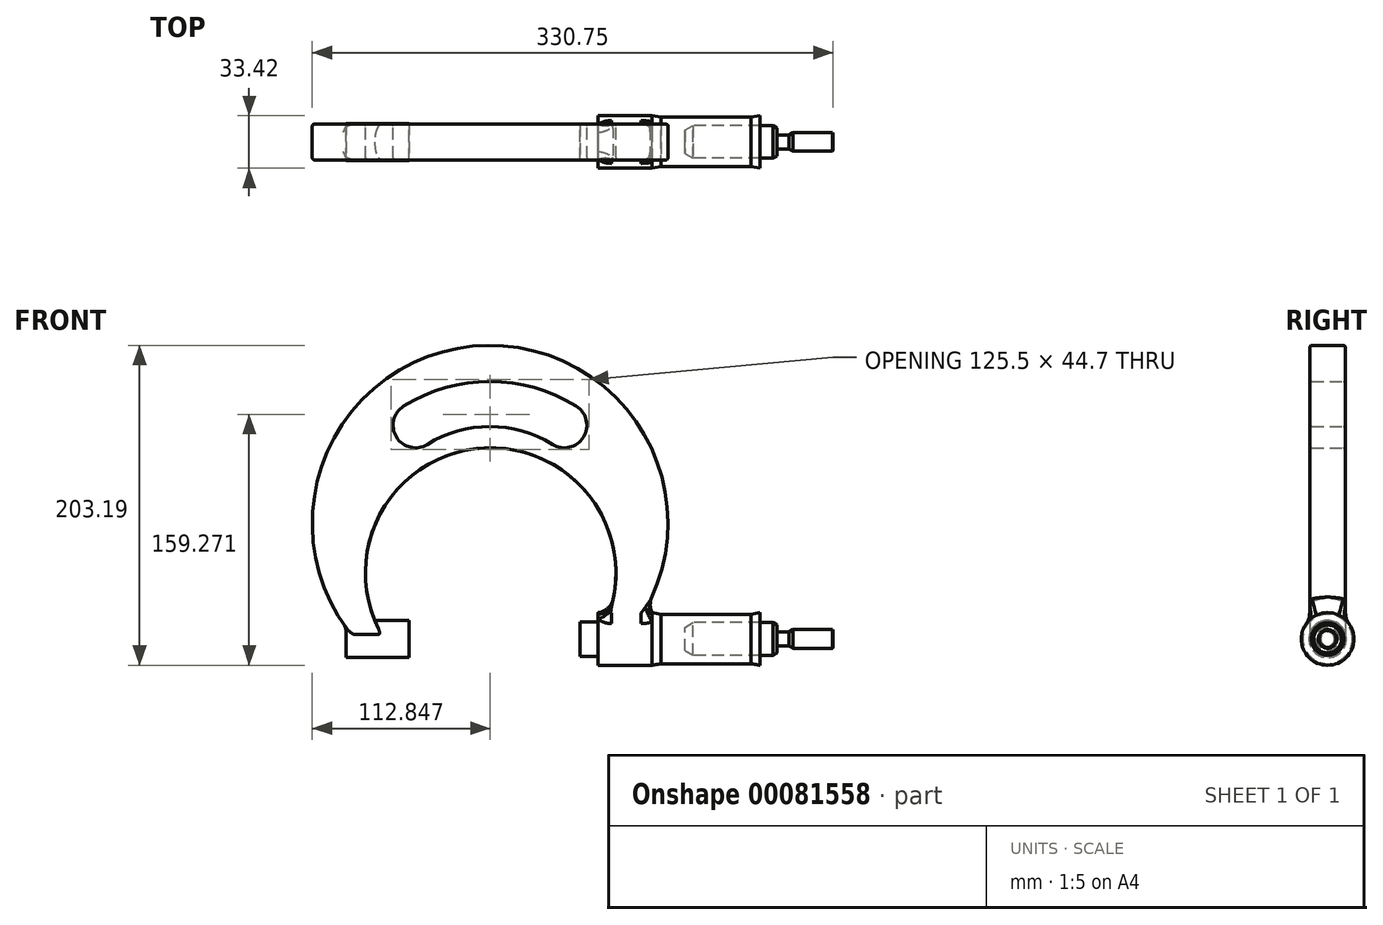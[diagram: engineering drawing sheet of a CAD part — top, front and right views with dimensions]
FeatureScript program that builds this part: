
annotation { "Feature Type Name" : "Feature", "Feature Type Description" : "" }
export const myFeature = defineFeature(function(context is Context, id is Id, definition is map)
    precondition{}
    {
        {
            var Q0;
            Q0=qCreatedBy(makeId("Front.planeOp"),FACE);
            var sketch = newSketch(context, id + "F0", { "sketchPlane" : qUnion([Q0])});
            skArc(sketch, "E0", {"start": v(0, 0) * mm, "mid": v(-38.1, 82.88) * mm, "end": v(-76.2, 0) * mm});
            skArc(sketch, "E1", {"start": v(-7.9, 0) * mm, "mid": v(-37.96, 53.97) * mm, "end": v(-68.04, 0) * mm});
            skLineSegment(sketch, "E2", {"start": v(-76.2, 0) * mm, "end": v(-68.04, 0) * mm});
            skLineSegment(sketch, "E3", {"start": v(-7.9, 0) * mm, "end": v(0, 0) * mm});
            skLineSegment(sketch, "E4.bottom", {"start": v(-76.2, 0) * mm, "end": v(-67.8, 0) * mm});
            skLineSegment(sketch, "E5", {"start": v(-38.1, 69.98) * mm, "end": v(-37.96, -37.66) * mm, "construction": true});
            skLineSegment(sketch, "E6", {"start": v(-89.8, 60.32) * mm, "end": v(20.51, 60.32) * mm, "construction": true});
            skArc(sketch, "E7", {"start": v(-17.15, 60.32) * mm, "mid": v(-38.14, 66.3) * mm, "end": v(-59.14, 60.32) * mm});
            skArc(sketch, "E8.0.startCap", {"start": v(-13.8, 65.71) * mm, "mid": v(-11.75, 56.97) * mm, "end": v(-20.5, 54.93) * mm});
            skArc(sketch, "E8.0.endCap", {"start": v(-55.79, 54.93) * mm, "mid": v(-64.53, 56.97) * mm, "end": v(-62.5, 65.71) * mm});
            skArc(sketch, "E8.0.left", {"start": v(-20.5, 54.93) * mm, "mid": v(-38.14, 59.96) * mm, "end": v(-55.79, 54.93) * mm});
            skArc(sketch, "E8.0.right", {"start": v(-13.8, 65.71) * mm, "mid": v(-38.14, 72.66) * mm, "end": v(-62.5, 65.71) * mm});
            skSolve(sketch);
        }
        {
            var Q0;
            Q0 = qSketchRegion(id + "F0", true);
            extrude(context, id + "F1", {"entities" : qUnion([Q0]), "depth" : 5.08 * mm, "hasSecondDirection" : true, "secondDirectionOppositeDirection" : true, "secondDirectionDepth" : 5.08 * mm});
        }
        {
            var Q0;
            Q0=makeQuery(id+"F1.opExtrude","CAP_FACE",FACE,{"disambiguationData":[OSD([sQuery(id+"F0.wireOp",EDGE,"E0"),sQuery(id+"F0.wireOp",EDGE,"E1"),sQuery(id+"F0.wireOp",EDGE,"E4.bottom"),sQuery(id+"F0.wireOp",EDGE,"E4.top"),sQuery(id+"F0.wireOp",EDGE,"E4.left"),sQuery(id+"F0.wireOp",EDGE,"E4.right"),sQuery(id+"F0.wireOp",EDGE,"VIkeURCC-5Tp6-DDTl-tPK2-hxNMprlm5AdZ.top"),sQuery(id+"F0.wireOp",EDGE,"VIkeURCC-5Tp6-DDTl-tPK2-hxNMprlm5AdZ.left"),sQuery(id+"F0.wireOp",EDGE,"VIkeURCC-5Tp6-DDTl-tPK2-hxNMprlm5AdZ.right"),sQuery(id+"F0.wireOp",EDGE,"E8.0.startCap"),sQuery(id+"F0.wireOp",EDGE,"E8.0.endCap"),sQuery(id+"F0.wireOp",EDGE,"E8.0.left"),sQuery(id+"F0.wireOp",EDGE,"E8.0.right")])],"isStart":true});
            var Q1;
            Q1=makeQuery(id+"F1.opExtrude","CAP_FACE",FACE,{"disambiguationData":[OSD([sQuery(id+"F0.wireOp",EDGE,"E0"),sQuery(id+"F0.wireOp",EDGE,"E1"),sQuery(id+"F0.wireOp",EDGE,"E4.bottom"),sQuery(id+"F0.wireOp",EDGE,"E4.top"),sQuery(id+"F0.wireOp",EDGE,"E4.left"),sQuery(id+"F0.wireOp",EDGE,"E4.right"),sQuery(id+"F0.wireOp",EDGE,"VIkeURCC-5Tp6-DDTl-tPK2-hxNMprlm5AdZ.top"),sQuery(id+"F0.wireOp",EDGE,"VIkeURCC-5Tp6-DDTl-tPK2-hxNMprlm5AdZ.left"),sQuery(id+"F0.wireOp",EDGE,"VIkeURCC-5Tp6-DDTl-tPK2-hxNMprlm5AdZ.right"),sQuery(id+"F0.wireOp",EDGE,"E8.0.startCap"),sQuery(id+"F0.wireOp",EDGE,"E8.0.endCap"),sQuery(id+"F0.wireOp",EDGE,"E8.0.left"),sQuery(id+"F0.wireOp",EDGE,"E8.0.right")])],"isStart":false});
            fillet(context, id + "F2", {"entities" : qUnion([Q0, Q1]), "radius" : 0.64 * mm, "tangentPropagation" : true, "allowEdgeOverflow" : false});
        }
        {
            var Q0;
            Q0=qCreatedBy(makeId("Right.planeOp"),FACE);
            var sketch = newSketch(context, id + "F3", { "sketchPlane" : qUnion([Q0])});
            skCircle(sketch, "E9", {"center": v(0, 0) * mm, "radius": 7.43 * mm});
            skSolve(sketch);
        }
        {
            var Q0;
            Q0 = qSketchRegion(id + "F3", true);
            extrude(context, id + "F4", {"entities" : qUnion([Q0]), "operationType" : NewBodyOperationType.ADD, "depth" : 7.62 * mm, "hasSecondDirection" : true, "secondDirectionOppositeDirection" : true, "secondDirectionDepth" : 7.62 * mm});
        }
        {
            var Q0;
            Q0=makeQuery(id+"F4.boolean.opBoolean","INTERSECT",EDGE,{"derivedFrom":[makeQuery(id+"F1.opExtrude","SWEPT_FACE",FACE,{"disambiguationData":[OSD([sQuery(id+"F0.wireOp",EDGE,"E0")])]}),makeQuery(id+"F4.opExtrude","SWEPT_FACE",FACE,{"disambiguationData":[OSD([sQuery(id+"F3.wireOp",EDGE,"E9")])]})]});
            var Q1;
            Q1=makeQuery(id+"F4.boolean.opBoolean","INTERSECT",EDGE,{"derivedFrom":[makeQuery(id+"F1.opExtrude","CAP_FACE",FACE,{"disambiguationData":[OSD([sQuery(id+"F0.wireOp",EDGE,"E0"),sQuery(id+"F0.wireOp",EDGE,"E1"),sQuery(id+"F0.wireOp",EDGE,"E4.bottom"),sQuery(id+"F0.wireOp",EDGE,"E3"),sQuery(id+"F0.wireOp",EDGE,"E8.0.startCap"),sQuery(id+"F0.wireOp",EDGE,"E8.0.endCap"),sQuery(id+"F0.wireOp",EDGE,"E8.0.left"),sQuery(id+"F0.wireOp",EDGE,"E8.0.right")])],"isStart":true}),makeQuery(id+"F4.opExtrude","SWEPT_FACE",FACE,{"disambiguationData":[OSD([sQuery(id+"F3.wireOp",EDGE,"E9")])]})]});
            var Q2;
            Q2=makeQuery(id+"F4.boolean.opBoolean","INTERSECT",EDGE,{"derivedFrom":[makeQuery(id+"F1.opExtrude","SWEPT_FACE",FACE,{"disambiguationData":[OSD([sQuery(id+"F0.wireOp",EDGE,"E1")])]}),makeQuery(id+"F4.opExtrude","SWEPT_FACE",FACE,{"disambiguationData":[OSD([sQuery(id+"F3.wireOp",EDGE,"E9")])]})]});
            var Q3;
            Q3=makeQuery(id+"F4.boolean.opBoolean","INTERSECT",EDGE,{"derivedFrom":[makeQuery(id+"F1.opExtrude","CAP_FACE",FACE,{"disambiguationData":[OSD([sQuery(id+"F0.wireOp",EDGE,"E0"),sQuery(id+"F0.wireOp",EDGE,"E1"),sQuery(id+"F0.wireOp",EDGE,"E4.bottom"),sQuery(id+"F0.wireOp",EDGE,"E3"),sQuery(id+"F0.wireOp",EDGE,"E8.0.startCap"),sQuery(id+"F0.wireOp",EDGE,"E8.0.endCap"),sQuery(id+"F0.wireOp",EDGE,"E8.0.left"),sQuery(id+"F0.wireOp",EDGE,"E8.0.right")])],"isStart":false}),makeQuery(id+"F4.opExtrude","SWEPT_FACE",FACE,{"disambiguationData":[OSD([sQuery(id+"F3.wireOp",EDGE,"E9")])]})]});
            fillet(context, id + "F5", {"entities" : qUnion([Q0, Q1, Q2, Q3]), "radius" : 5.08 * mm, "tangentPropagation" : true, "allowEdgeOverflow" : false});
        }
        {
            var Q0;
            Q0=makeQuery(id+"F4.opExtrude","CAP_FACE",FACE,{"disambiguationData":[OSD([sQuery(id+"F3.wireOp",EDGE,"E9")])],"isStart":false});
            extrude(context, id + "F6", {"entities" : qUnion([Q0]), "operationType" : NewBodyOperationType.ADD, "depth" : 2.54 * mm, "hasDraft" : true, "draftAngle" : 10 * degree, "draftPullDirection" : true});
        }
        {
            var Q0;
            Q0=makeQuery(id+"F6.opExtrude","CAP_FACE",FACE,{"disambiguationData":[OSD([sQuery(id+"F3.wireOp",EDGE,"E9")])],"isStart":false});
            extrude(context, id + "F7", {"entities" : qUnion([Q0]), "operationType" : NewBodyOperationType.ADD, "depth" : 25.4 * mm});
        }
        {
            var Q0;
            Q0=makeQuery(id+"F7.opExtrude","CAP_FACE",FACE,{"disambiguationData":[OSD([sQuery(id+"F3.wireOp",EDGE,"E9")])],"isStart":false});
            extrude(context, id + "F8", {"entities" : qUnion([Q0]), "operationType" : NewBodyOperationType.ADD, "depth" : 2.54 * mm, "hasDraft" : true, "draftAngle" : 10 * degree});
        }
        {
            var Q0;
            Q0=makeQuery(id+"F8.opExtrude","CAP_FACE",FACE,{"disambiguationData":[OSD([sQuery(id+"F3.wireOp",EDGE,"E9")])],"isStart":false});
            extrude(context, id + "F9", {"entities" : qUnion([Q0]), "depth" : 5.08 * mm, "hasDraft" : true, "draftAngle" : 30 * degree});
        }
        {
            var Q0;
            Q0=makeQuery(id+"F9.opExtrude","CAP_FACE",FACE,{"disambiguationData":[OSD([sQuery(id+"F3.wireOp",EDGE,"E9")])],"isStart":false});
            extrude(context, id + "F10", {"entities" : qUnion([Q0]), "operationType" : NewBodyOperationType.ADD, "depth" : 25.4 * mm});
        }
        {
            var Q0;
            Q0=makeQuery(id+"F10.opExtrude","CAP_FACE",FACE,{"disambiguationData":[OSD([sQuery(id+"F3.wireOp",EDGE,"E9")])],"isStart":false});
            extrude(context, id + "F11", {"entities" : qUnion([Q0]), "operationType" : NewBodyOperationType.ADD, "depth" : 25.4 * mm});
        }
        {
            var Q0;
            Q0=makeQuery(id+"F11.opExtrude","CAP_FACE",FACE,{"disambiguationData":[OSD([sQuery(id+"F3.wireOp",EDGE,"E9")])],"isStart":false});
            extrude(context, id + "F12", {"entities" : qUnion([Q0]), "operationType" : NewBodyOperationType.ADD, "depth" : 2.54 * mm, "hasDraft" : true, "draftAngle" : 30 * degree, "draftPullDirection" : true});
        }
        {
            var Q0;
            Q0=makeQuery(id+"F12.opExtrude","CAP_FACE",FACE,{"disambiguationData":[OSD([sQuery(id+"F3.wireOp",EDGE,"E9")])],"isStart":false});
            var sketch = newSketch(context, id + "F13", { "sketchPlane" : qUnion([Q0])});
            skCircle(sketch, "E10", {"center": v(0, 0) * mm, "radius": 4.45 * mm});
            skSolve(sketch);
        }
        {
            var Q0;
            Q0 = qSketchRegion(id + "F13", true);
            extrude(context, id + "F14", {"entities" : qUnion([Q0]), "operationType" : NewBodyOperationType.ADD, "depth" : 7.62 * mm});
        }
        {
            var Q0;
            Q0=makeQuery(id+"F14.opExtrude","CAP_FACE",FACE,{"disambiguationData":[OSD([sQuery(id+"F13.wireOp",EDGE,"E10")])],"isStart":false});
            extrude(context, id + "F15", {"entities" : qUnion([Q0]), "operationType" : NewBodyOperationType.ADD, "depth" : 2.54 * mm, "hasDraft" : true, "draftAngle" : 30 * degree});
        }
        {
            var Q0;
            Q0=makeQuery(id+"F15.opExtrude","CAP_FACE",FACE,{"disambiguationData":[OSD([sQuery(id+"F13.wireOp",EDGE,"E10")])],"isStart":false});
            extrude(context, id + "F16", {"entities" : qUnion([Q0]), "operationType" : NewBodyOperationType.ADD, "depth" : 25.4 * mm});
        }
        {
            var Q0;
            Q0=makeQuery(id+"F4.opExtrude","CAP_FACE",FACE,{"disambiguationData":[OSD([sQuery(id+"F3.wireOp",EDGE,"E9")])],"isStart":true});
            cPlane(context, id + "F17", {"entities" : qUnion([Q0]), "cplaneType" : CPlaneType.OFFSET, "offset" : 71.12 * mm, "width" : 152.4 * mm, "height" : 152.4 * mm});
        }
        {
            var Q0;
            Q0=qCreatedBy(id+"F17.planeOp",FACE);
            var sketch = newSketch(context, id + "F18", { "sketchPlane" : qUnion([Q0])});
            skCircle(sketch, "E11", {"center": v(0, 0) * mm, "radius": 5.24 * mm});
            skSolve(sketch);
        }
        {
            var Q0;
            Q0 = qSketchRegion(id + "F18", true);
            extrude(context, id + "F19", {"entities" : qUnion([Q0]), "operationType" : NewBodyOperationType.ADD, "oppositeDirection" : true, "depth" : 17.78 * mm});
        }
        {
            var Q0;
            {var subQ0=sQuery(id+"F0.wireOp",EDGE,"E4.bottom");var subQ1=sQuery(id+"F0.wireOp",EDGE,"E1");Q0=makeQuery(id+"F19.boolean.opBoolean","INTERSECT",EDGE,{"derivedFrom":[makeQuery(id+"F4.boolean.opBoolean","SPLIT",FACE,{"disambiguationData":[TD([makeQuery(id+"F1.opExtrude","SWEPT_FACE",FACE,{"disambiguationData":[OSD([subQ0])]})])],"derivedFrom":makeQuery(id+"F1.opExtrude","SWEPT_FACE",FACE,{"disambiguationData":[OSD([subQ1])]})}),makeQuery(id+"F19.opExtrude","SWEPT_FACE",FACE,{"disambiguationData":[OSD([sQuery(id+"F18.wireOp",EDGE,"E11")])]})]});}
            var Q1;
            Q1=makeQuery(id+"F19.boolean.opBoolean","INTERSECT",EDGE,{"derivedFrom":[makeQuery(id+"F1.opExtrude","SWEPT_FACE",FACE,{"disambiguationData":[OSD([sQuery(id+"F0.wireOp",EDGE,"E0")])]}),makeQuery(id+"F19.opExtrude","CAP_FACE",FACE,{"disambiguationData":[OSD([sQuery(id+"F18.wireOp",EDGE,"E11")])],"isStart":true})]});
            fillet(context, id + "F20", {"entities" : qUnion([Q0, Q1]), "radius" : 5.08 * mm, "tangentPropagation" : true, "allowEdgeOverflow" : false});
        }
        {
            var Q0;
            Q0=makeQuery(id+"F4.opExtrude","CAP_FACE",FACE,{"disambiguationData":[OSD([sQuery(id+"F3.wireOp",EDGE,"E9")])],"isStart":true});
            var sketch = newSketch(context, id + "F21", { "sketchPlane" : qUnion([Q0])});
            skCircle(sketch, "E12", {"center": v(0, 0) * mm, "radius": 4.86 * mm});
            skSolve(sketch);
        }
        {
            var Q0;
            Q0 = qSketchRegion(id + "F21", true);
            extrude(context, id + "F22", {"entities" : qUnion([Q0]), "operationType" : NewBodyOperationType.ADD, "depth" : 5.08 * mm});
        }
        {
            var Q0;
            Q0=makeQuery(id+"F16.opExtrude","CAP_EDGE",EDGE,{"disambiguationData":[OSD([sQuery(id+"F13.wireOp",EDGE,"E10")])],"isStart":false});
            chamfer(context, id + "F23", {"entities" : qUnion([Q0]), "width" : 0.5 * mm, "tangentPropagation" : true});
        }
        {
            var Q0;
            Q0=makeQuery(id+"F1.opExtrude","SWEPT_BODY",BODY,{"disambiguationData":[OSD([sQuery(id+"F0.wireOp",EDGE,"E0"),sQuery(id+"F0.wireOp",EDGE,"E1"),sQuery(id+"F0.wireOp",EDGE,"E4.bottom"),sQuery(id+"F0.wireOp",EDGE,"E3"),sQuery(id+"F0.wireOp",EDGE,"E8.0.startCap"),sQuery(id+"F0.wireOp",EDGE,"E8.0.endCap"),sQuery(id+"F0.wireOp",EDGE,"E8.0.left"),sQuery(id+"F0.wireOp",EDGE,"E8.0.right")])]});
            var Q1;
            Q1=qCreatedBy(makeId("Origin.pointOp"),VERTEX);
            transform(context, id + "F24", {"entities" : qUnion([Q0]), "transformType" : TransformType.SCALE_UNIFORMLY, "scale" : 1.5, "scalePoint" : qUnion([Q1]), "makeCopy" : false});
        }
        {
            var Q0;
            Q0=makeQuery(id+"F1.opExtrude","SWEPT_BODY",BODY,{"disambiguationData":[OSD([sQuery(id+"F0.wireOp",EDGE,"E0"),sQuery(id+"F0.wireOp",EDGE,"E1"),sQuery(id+"F0.wireOp",EDGE,"E4.bottom"),sQuery(id+"F0.wireOp",EDGE,"E3"),sQuery(id+"F0.wireOp",EDGE,"E8.0.startCap"),sQuery(id+"F0.wireOp",EDGE,"E8.0.endCap"),sQuery(id+"F0.wireOp",EDGE,"E8.0.left"),sQuery(id+"F0.wireOp",EDGE,"E8.0.right")])]});
            var Q1;
            Q1=qCreatedBy(makeId("Origin.pointOp"),VERTEX);
            transform(context, id + "F25", {"entities" : qUnion([Q0]), "transformType" : TransformType.SCALE_UNIFORMLY, "scale" : 1.5, "scalePoint" : qUnion([Q1]), "makeCopy" : false});
        }
    });
